# Revit family: Pressure_Reducing_Valve-Zurn_Wilkins-Model_NR3XLDUPEX-(12-1_Inch)
name_source: partatom
category: Pipe Accessories
units: mm (PartAtom-declared; Revit-internal decimal feet)

## family parameters
Always vertical = Yes
Cut with Voids When Loaded = No
OmniClass Number = 23.65.55.14.17
OmniClass Title = Adjusting/Controlling Valves for Liquid Services
Part Type = Valve - Breaks Into
Round Connector Dimension = Use Radius
Shared = No
Work Plane-Based = No

## types (3) — shared parameters
Assembly Code = D2020300
Bell Base Length = 0' - 0 3/16"
Bell Base Radius = 0' - 1 1/32"
Bell Blend Radius = 0' - 0 3/4"
Bell Hex Radius = 0' - 0 13/16"
Bell Upper Base Length = 0' - 1 3/16"
Bell Upper Base Radius = 0' - 0 7/8"
Body Top Length = 0' - 1 5/32"
Body Top Seat Bell Radius = 0' - 1 1/4"
DIM B - Overall Height = 0' - 6 1/4"
DIM C - Body Center to Tail Length = 0' - 1 1/8"
DIM D - Bell base diameter = 0' - 2 1/2"
Default Elevation = 0' - 0"
Description = Water Pressure Reducing Valve with Integral By-pass check Valve and Strainer
Factory Preset Pressure = 50.00 psi
Flow Rate (GPM) = 0 GPM
Main Material = Paint - Zurn - Bronze
Manufacturer = Zurn Water, LLC
Manufacturer Brand = Zurn Wilkins
Max Working Water Pressure = 400.00 psi
Max Working Water Temperature = 140 °F
Model = NR3XLDUPEX
Modified Date = 08/22/2025
Product Documentation Link = https://files.zurn.com
Product Installation Sheet URL = https://files.zurn.com
Product Page URL = https://www.zurn.com
Product data URL = https://www.bimobject.com
Reduced Pressure Range = 15 to 75 psi
Repair Parts URL = https://files.zurn.com
Width = 0' - 0"
bottom of pex barb fitting = 0' - 0 9/32"
pex length = 0' - 1"
top of pex barb fitting = 0' - 0 11/32"

## per-type parameters (varying)
| type | Body Base Tail Radius | Body Radius | Body Seat Bell Length | Body Tail Radius | Body Thread Radius | Body Top Radius | Body Width | DIM A - LESS UNION (Main body length) | Dimension A | Horizontal pex alignment | MR End to hex | MR hex nut thickness | MR hex nut width | MR pex pipe dia | Nominal Diameter | Nominal Radius | Nut Length | Nut Size | Overall length of the valve | Polygon diameter | Product Weight (lbs) | Tailpiece radius | URL | pex fitting |
| 1-NR3XLDUPEX (1" NR3XLDUPEX) | 0' - 0 13/16" | 0' - 0 27/32" | 0' - 0 15/32" | 0' - 0 7/16" | 0' - 0 7/8" | 0' - 1" | 0' - 0 17/32" | 0' - 4" | 0' - 4 15/16" | 0' - 0 3/4" | 0' - 0 15/16" | 0' - 0 21/32" | 0' - 2" | 0' - 1" | 0' - 1" | 0' - 0 1/2" | 0' - 2 1/4" | Nut : 1 inch | 0' - 6 7/16" | 0' - 2 1/4" | 5 | 0' - 0 3/4" | http://www.zurn.com | pex fitting : 1 inch pex fitting |
| 34-NR3XLDUPEX (3/4" NR3XLDUPEX) | 0' - 0 5/8" | 0' - 0 11/16" | 0' - 0 1/2" | 0' - 0 11/32" | 0' - 0 13/16" | 0' - 1 1/16" | 0' - 0 3/8" | 0' - 3 1/2" | 0' - 4 7/16" | 0' - 0 21/32" | 0' - 0 25/32" | 0' - 0 5/8" | 0' - 1 3/4" | 0' - 0 3/4" | 0' - 0 3/4" | 0' - 0 3/8" | 0' - 2 1/8" | Nut : 3/4 inch | 0' - 5 25/32" | 0' - 2 1/4" | 3 | 0' - 0 5/8" | http://www.zurn.com | pex fitting : 3/4 inch pex fitting |
| 12-NR3XLDUPEX (1/2" NR3XLDUPEX) | 0' - 0 5/8" | 0' - 0 11/16" | 0' - 0 15/32" | 0' - 0 7/16" | 0' - 0 13/16" | 0' - 1 1/16" | 0' - 0 7/16" | 0' - 3 1/2" | 0' - 4 3/8" | 0' - 0 9/16" | 0' - 0 31/32" | 0' - 0 5/8" | 0' - 1 3/4" | 0' - 0 1/2" | 0' - 0 1/2" | 0' - 0 1/4" | 0' - 2 1/16" | Nut : 1/2 inch | 0' - 6 1/32" | 0' - 1 3/4" | 3 | 0' - 0 1/2" | https://www.zurn.com | pex fitting : 1/2 inch pex fitting |

## geometry (parser evidence)
native form markers: Blend x1, Sweep x7
no freeform markers — native parametric forms only
